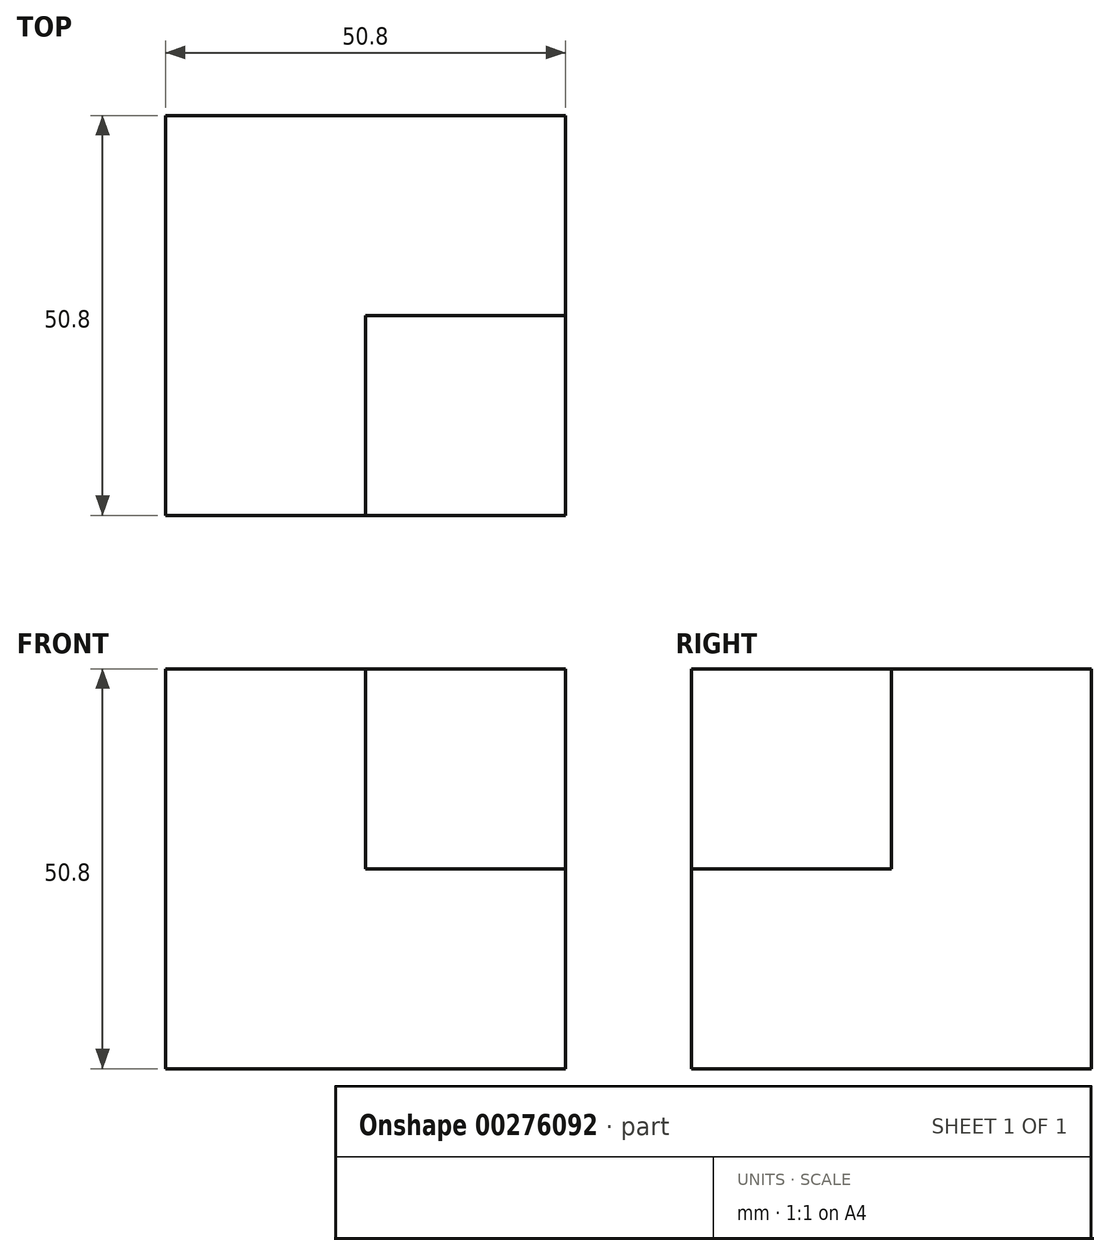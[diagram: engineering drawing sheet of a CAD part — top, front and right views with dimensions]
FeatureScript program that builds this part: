
annotation { "Feature Type Name" : "Feature", "Feature Type Description" : "" }
export const myFeature = defineFeature(function(context is Context, id is Id, definition is map)
    precondition{}
    {
        {
            var Q0;
            Q0=qCreatedBy(makeId("Front.planeOp"),FACE);
            var sketch = newSketch(context, id + "F0", { "sketchPlane" : qUnion([Q0])});
            skLineSegment(sketch, "E0", {"start": v(0, 0) * mm, "end": v(-50.8, 0) * mm});
            skLineSegment(sketch, "E1", {"start": v(-50.8, 0) * mm, "end": v(-50.8, 50.8) * mm});
            skLineSegment(sketch, "E2", {"start": v(-50.8, 50.8) * mm, "end": v(0, 50.8) * mm});
            skLineSegment(sketch, "E3", {"start": v(0, 50.8) * mm, "end": v(0, 0) * mm});
            skSolve(sketch);
        }
        {
            var Q0;
            Q0=makeQuery(id+"F0.imprint","IMPRINT",FACE,{"disambiguationData":[TD([[makeQuery(id+"F0.imprint","IMPRINT",EDGE,{"derivedFrom":sQuery(id+"F0.wireOp",EDGE,"E0")}),-1.0]])]});
            var Q1;
            Q1 = qSketchRegion(id + "F2", true);
            extrude(context, id + "F1", {"entities" : qUnion([Q0, Q1]), "depth" : 50.8 * mm});
        }
        {
            var Q0;
            Q0=makeQuery(id+"F1.opExtrude","SWEPT_FACE",FACE,{"disambiguationData":[OSD([sQuery(id+"F0.wireOp",EDGE,"E2")])]});
            var sketch = newSketch(context, id + "F2", { "sketchPlane" : qUnion([Q0])});
            skLineSegment(sketch, "E4.bottom", {"start": v(0, -50.8) * mm, "end": v(-25.4, -50.8) * mm});
            skLineSegment(sketch, "E4.top", {"start": v(0, -25.4) * mm, "end": v(-25.4, -25.4) * mm});
            skLineSegment(sketch, "E4.left", {"start": v(0, -50.8) * mm, "end": v(0, -25.4) * mm});
            skLineSegment(sketch, "E4.right", {"start": v(-25.4, -50.8) * mm, "end": v(-25.4, -25.4) * mm});
            skSolve(sketch);
        }
        {
            var Q0;
            Q0=makeQuery(id+"F2.imprint","IMPRINT",FACE,{"disambiguationData":[TD([[makeQuery(id+"F2.imprint","IMPRINT",EDGE,{"derivedFrom":sQuery(id+"F2.wireOp",EDGE,"E4.bottom")}),1.0]])]});
            extrude(context, id + "F3", {"entities" : qUnion([Q0]), "operationType" : NewBodyOperationType.REMOVE, "oppositeDirection" : true, "depth" : 25.4 * mm});
        }
    });
